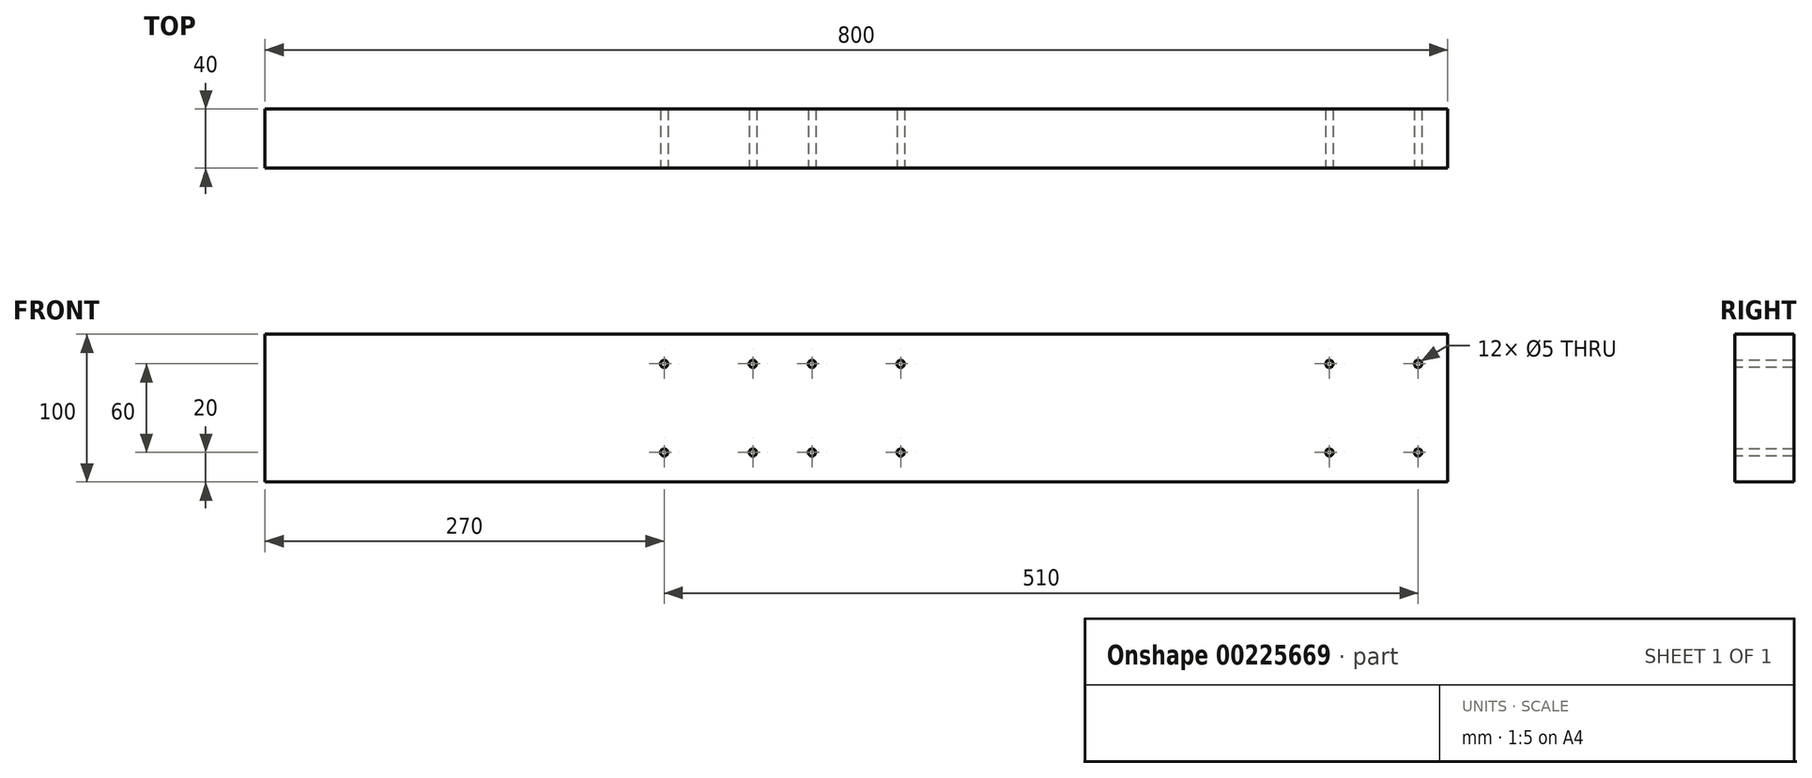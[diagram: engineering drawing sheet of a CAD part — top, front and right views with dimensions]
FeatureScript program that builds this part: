
annotation { "Feature Type Name" : "Feature", "Feature Type Description" : "" }
export const myFeature = defineFeature(function(context is Context, id is Id, definition is map)
    precondition{}
    {
        {
            var Q0;
            Q0=qCreatedBy(makeId("Front.planeOp"),FACE);
            var sketch = newSketch(context, id + "F0", { "sketchPlane" : qUnion([Q0])});
            skLineSegment(sketch, "E0.bottom", {"start": v(-400, 50) * mm, "end": v(400, 50) * mm});
            skLineSegment(sketch, "E0.top", {"start": v(-400, -50) * mm, "end": v(400, -50) * mm});
            skLineSegment(sketch, "E0.left", {"start": v(-400, 50) * mm, "end": v(-400, -50) * mm});
            skLineSegment(sketch, "E0.right", {"start": v(400, 50) * mm, "end": v(400, -50) * mm});
            skLineSegment(sketch, "E1", {"start": v(0, 50) * mm, "end": v(0, -50) * mm, "construction": true});
            skLineSegment(sketch, "E2", {"start": v(-400, 0) * mm, "end": v(400, 0) * mm, "construction": true});
            skSolve(sketch);
        }
        {
            var Q0;
            Q0=makeQuery(id+"F0.imprint","IMPRINT",FACE,{"disambiguationData":[TD([[makeQuery(id+"F0.imprint","IMPRINT",EDGE,{"derivedFrom":sQuery(id+"F0.wireOp",EDGE,"E0.bottom")}),-1.0]])]});
            extrude(context, id + "F1", {"entities" : qUnion([Q0]), "endBound" : BoundingType.SYMMETRIC, "depth" : 40 * mm});
        }
        {
            var Q0;
            Q0=makeQuery(id+"F1.opExtrude","CAP_FACE",FACE,{"disambiguationData":[OSD([sQuery(id+"F0.wireOp",EDGE,"E0.bottom"),sQuery(id+"F0.wireOp",EDGE,"E0.top"),sQuery(id+"F0.wireOp",EDGE,"E0.left"),sQuery(id+"F0.wireOp",EDGE,"E0.right")])],"isStart":false});
            var sketch = newSketch(context, id + "F2", { "sketchPlane" : qUnion([Q0])});
            skPoint(sketch, "E3", {"position": v(380, 30) * mm});
            skPoint(sketch, "E4", {"position": v(380, -30) * mm});
            skPoint(sketch, "E5", {"position": v(320, 30) * mm});
            skPoint(sketch, "E6", {"position": v(320, -30) * mm});
            skLineSegment(sketch, "E7", {"start": v(-50, 50) * mm, "end": v(-50, -50) * mm, "construction": true});
            skPoint(sketch, "E8", {"position": v(-70, 30) * mm});
            skPoint(sketch, "E9", {"position": v(-70, -30) * mm});
            skPoint(sketch, "E10", {"position": v(-130, 30) * mm});
            skPoint(sketch, "E11", {"position": v(-130, -30) * mm});
            skPoint(sketch, "E12", {"position": v(30, 30) * mm});
            skPoint(sketch, "E13", {"position": v(30, -30) * mm});
            skPoint(sketch, "E14", {"position": v(-30, 30) * mm});
            skPoint(sketch, "E15", {"position": v(-30, -30) * mm});
            skSolve(sketch);
        }
        {
            var Q0;
            Q0=sQuery(id+"F2.wireOp",VERTEX,"E5");
            var Q1;
            Q1=sQuery(id+"F2.wireOp",VERTEX,"E3");
            var Q2;
            Q2=sQuery(id+"F2.wireOp",VERTEX,"E6");
            var Q3;
            Q3=sQuery(id+"F2.wireOp",VERTEX,"E4");
            var Q4;
            Q4=sQuery(id+"F2.wireOp",VERTEX,"E10");
            var Q5;
            Q5=sQuery(id+"F2.wireOp",VERTEX,"E8");
            var Q6;
            Q6=sQuery(id+"F2.wireOp",VERTEX,"E11");
            var Q7;
            Q7=sQuery(id+"F2.wireOp",VERTEX,"E9");
            var Q8;
            Q8=sQuery(id+"F2.wireOp",VERTEX,"E14");
            var Q9;
            Q9=sQuery(id+"F2.wireOp",VERTEX,"E12");
            var Q10;
            Q10=sQuery(id+"F2.wireOp",VERTEX,"E15");
            var Q11;
            Q11=sQuery(id+"F2.wireOp",VERTEX,"E13");
            var Q12;
            Q12=makeQuery(id+"F1.opExtrude","SWEPT_BODY",BODY,{"disambiguationData":[OSD([sQuery(id+"F0.wireOp",EDGE,"E0.bottom"),sQuery(id+"F0.wireOp",EDGE,"E0.top"),sQuery(id+"F0.wireOp",EDGE,"E0.left"),sQuery(id+"F0.wireOp",EDGE,"E0.right")])]});
            hole(context, id + "F3", {"style" : HoleStyle.SIMPLE, "endStyle" : HoleEndStyle.THROUGH, "holeDiameter" : 5 * mm, "locations" : qUnion([Q0, Q1, Q2, Q3, Q4, Q5, Q6, Q7, Q8, Q9, Q10, Q11]), "scope" : qUnion([Q12]), "isTappedThrough" : true});
        }
    });
